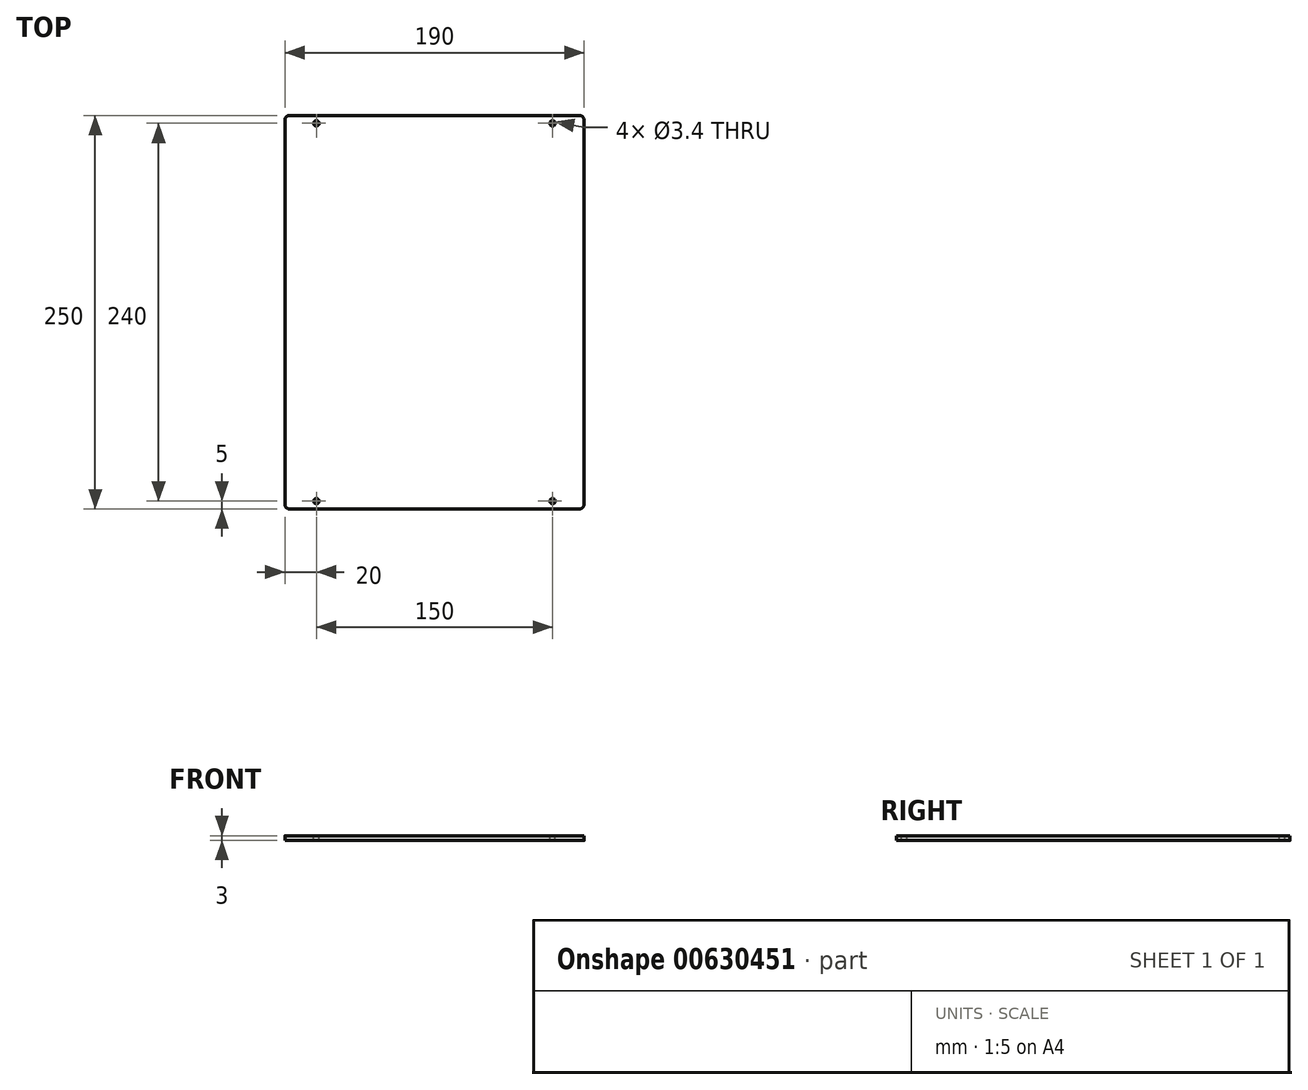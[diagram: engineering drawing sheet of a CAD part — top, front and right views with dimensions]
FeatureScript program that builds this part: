
annotation { "Feature Type Name" : "Feature", "Feature Type Description" : "" }
export const myFeature = defineFeature(function(context is Context, id is Id, definition is map)
    precondition{}
    {
        {
            var Q0;
            Q0=qCreatedBy(makeId("Top.planeOp"),FACE);
            var sketch = newSketch(context, id + "F0", { "sketchPlane" : qUnion([Q0])});
            skLineSegment(sketch, "E0.bottom", {"start": v(95, 125) * mm, "end": v(-95, 125) * mm});
            skLineSegment(sketch, "E0.top", {"start": v(95, -125) * mm, "end": v(-95, -125) * mm});
            skLineSegment(sketch, "E0.left", {"start": v(95, 125) * mm, "end": v(95, -125) * mm});
            skLineSegment(sketch, "E0.right", {"start": v(-95, 125) * mm, "end": v(-95, -125) * mm});
            skPoint(sketch, "E0.middle", {"position": v(0, 0) * mm});
            skCircle(sketch, "E1", {"center": v(-75, 120) * mm, "radius": 1.7 * mm});
            skCircle(sketch, "E2", {"center": v(75, 120) * mm, "radius": 1.7 * mm});
            skCircle(sketch, "E3", {"center": v(-75, -120) * mm, "radius": 1.7 * mm});
            skCircle(sketch, "E4", {"center": v(75, -120) * mm, "radius": 1.7 * mm});
            skSolve(sketch);
        }
        {
            var Q0;
            Q0=qSketchRegion(id+"F0",true);
            extrude(context, id + "F1", {"entities" : qUnion([Q0]), "oppositeDirection" : true, "depth" : 3 * mm});
        }
        {
            var Q0;
            Q0=makeQuery(id+"F1.opExtrude","SWEPT_EDGE",EDGE,{"disambiguationData":[OSD([sQuery(id+"F0.wireOp",EDGE,"E0.bottom"),sQuery(id+"F0.wireOp",EDGE,"E0.left")])]});
            var Q1;
            Q1=makeQuery(id+"F1.opExtrude","SWEPT_EDGE",EDGE,{"disambiguationData":[OSD([sQuery(id+"F0.wireOp",EDGE,"E0.bottom"),sQuery(id+"F0.wireOp",EDGE,"E0.right")])]});
            var Q2;
            Q2=makeQuery(id+"F1.opExtrude","SWEPT_EDGE",EDGE,{"disambiguationData":[OSD([sQuery(id+"F0.wireOp",EDGE,"E0.top"),sQuery(id+"F0.wireOp",EDGE,"E0.left")])]});
            var Q3;
            Q3=makeQuery(id+"F1.opExtrude","SWEPT_EDGE",EDGE,{"disambiguationData":[OSD([sQuery(id+"F0.wireOp",EDGE,"E0.top"),sQuery(id+"F0.wireOp",EDGE,"E0.right")])]});
            fillet(context, id + "F2", {"entities" : qUnion([Q0, Q1, Q2, Q3]), "radius" : 3 * mm, "tangentPropagation" : true, "allowEdgeOverflow" : false});
        }
    });
